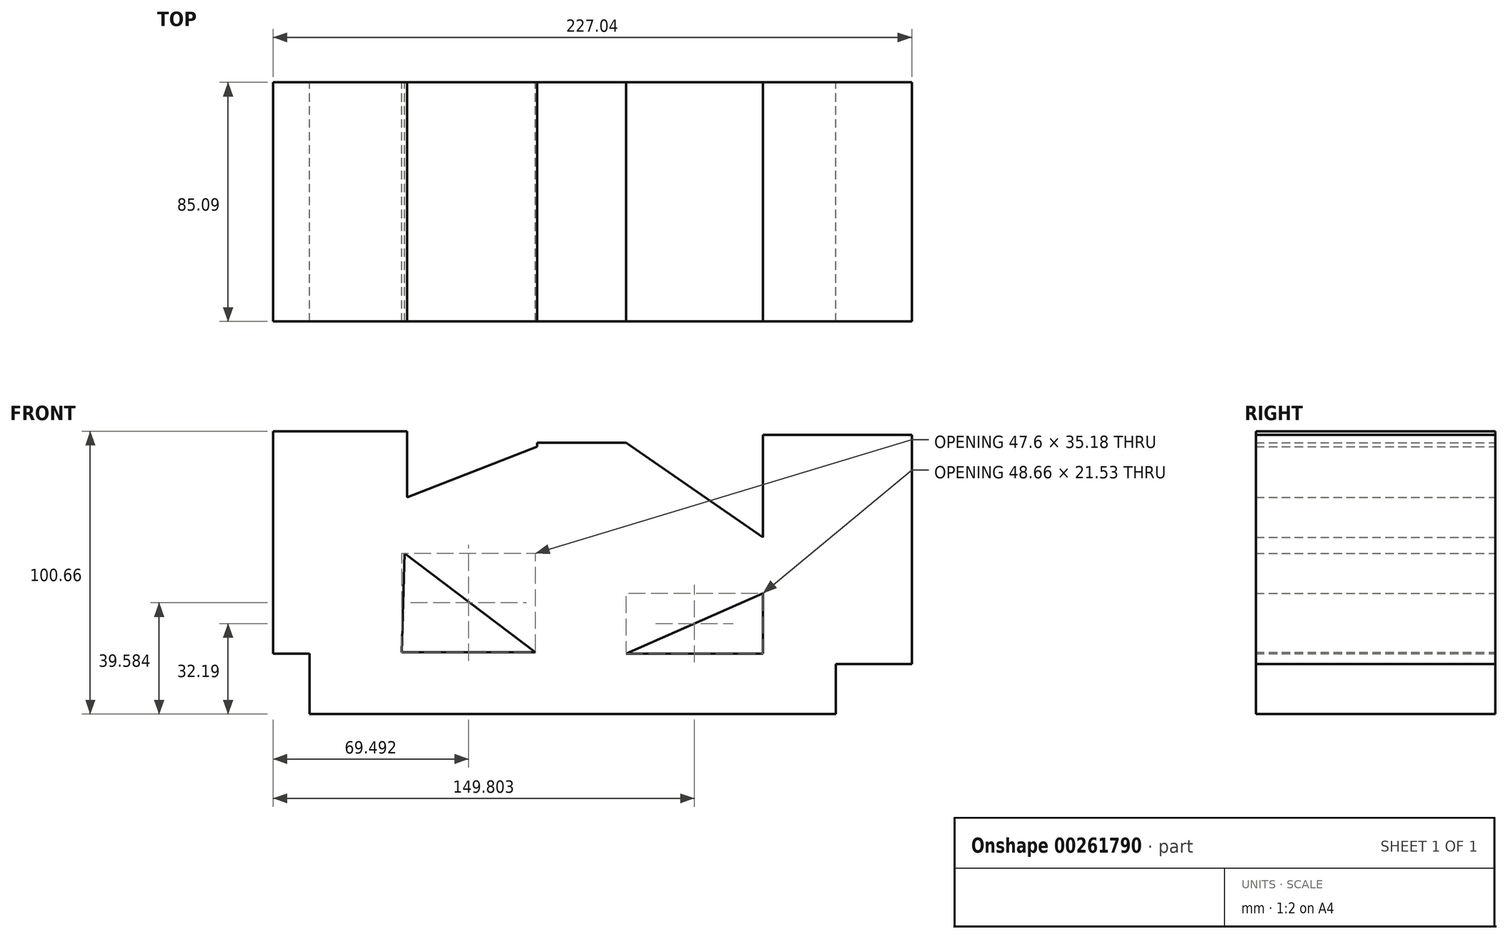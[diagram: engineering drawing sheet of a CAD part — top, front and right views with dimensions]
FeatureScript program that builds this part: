
annotation { "Feature Type Name" : "Feature", "Feature Type Description" : "" }
export const myFeature = defineFeature(function(context is Context, id is Id, definition is map)
    precondition{}
    {
        {
            var Q0;
            Q0=qCreatedBy(makeId("Front.planeOp"),FACE);
            var sketch = newSketch(context, id + "F0", { "sketchPlane" : qUnion([Q0])});
            skLineSegment(sketch, "E0", {"start": v(-47.14, -5.82) * mm, "end": v(-112.45, -5.82) * mm});
            skLineSegment(sketch, "E1", {"start": v(-112.45, -5.82) * mm, "end": v(-112.45, -27.81) * mm});
            skLineSegment(sketch, "E2", {"start": v(-112.45, -27.81) * mm, "end": v(74.56, -27.81) * mm});
            skLineSegment(sketch, "E3", {"start": v(74.56, -27.81) * mm, "end": v(74.56, -6.39) * mm});
            skLineSegment(sketch, "E4", {"start": v(74.56, -6.39) * mm, "end": v(0, -6.39) * mm});
            skLineSegment(sketch, "E5", {"start": v(-47.14, -5.82) * mm, "end": v(-31.62, -5.82) * mm});
            skLineSegment(sketch, "E6", {"start": v(0, -6.39) * mm, "end": v(0, 68.7) * mm});
            skLineSegment(sketch, "E7", {"start": v(0, 68.7) * mm, "end": v(-31.62, 68.7) * mm});
            skLineSegment(sketch, "E8", {"start": v(-31.62, 68.7) * mm, "end": v(-31.62, -5.82) * mm});
            skLineSegment(sketch, "E9", {"start": v(0, 68.7) * mm, "end": v(48.67, 35.1) * mm});
            skLineSegment(sketch, "E10", {"start": v(48.67, 35.1) * mm, "end": v(48.67, 15.15) * mm});
            skLineSegment(sketch, "E11", {"start": v(48.67, 15.15) * mm, "end": v(0, -6.39) * mm});
            skLineSegment(sketch, "E12", {"start": v(-31.52, -6.32) * mm, "end": v(-78.68, 29.36) * mm});
            skLineSegment(sketch, "E13", {"start": v(-78.68, 29.36) * mm, "end": v(-77.8, 49.3) * mm});
            skLineSegment(sketch, "E14", {"start": v(-77.8, 49.3) * mm, "end": v(-28.25, 68.7) * mm});
            skLineSegment(sketch, "E15", {"start": v(48.67, 15.15) * mm, "end": v(48.67, -6.39) * mm});
            skPoint(sketch, "E15.endSnap0", {"position": v(37.28, -6.39) * mm});
            skLineSegment(sketch, "E16", {"start": v(48.67, -6.39) * mm, "end": v(48.67, 71.46) * mm});
            skLineSegment(sketch, "E17", {"start": v(48.67, 71.46) * mm, "end": v(101.57, 71.46) * mm});
            skLineSegment(sketch, "E18", {"start": v(101.57, 71.46) * mm, "end": v(101.57, -10.05) * mm});
            skLineSegment(sketch, "E19", {"start": v(101.57, -10.05) * mm, "end": v(48.67, -10.05) * mm});
            skLineSegment(sketch, "E20", {"start": v(48.67, -10.05) * mm, "end": v(48.67, 0) * mm});
            skLineSegment(sketch, "E21", {"start": v(48.67, 0) * mm, "end": v(48.67, -6.39) * mm});
            skLineSegment(sketch, "E22", {"start": v(-77.8, 49.3) * mm, "end": v(-77.8, 72.85) * mm});
            skLineSegment(sketch, "E23", {"start": v(-77.8, 72.85) * mm, "end": v(-125.47, 72.85) * mm});
            skLineSegment(sketch, "E24", {"start": v(-125.47, 72.85) * mm, "end": v(-125.47, -6.39) * mm});
            skLineSegment(sketch, "E25", {"start": v(-125.47, -6.39) * mm, "end": v(-79.8, -6.39) * mm});
            skPoint(sketch, "E25.endSnap0", {"position": v(-79.8, -5.82) * mm});
            skLineSegment(sketch, "E26", {"start": v(-79.8, -6.39) * mm, "end": v(-78.68, 29.36) * mm});
            skSolve(sketch);
        }
        {
            var Q0;
            Q0 = qSketchRegion(id + "F0", true);
            extrude(context, id + "F1", {"entities" : qUnion([Q0]), "depth" : 85.1 * mm});
        }
    });
